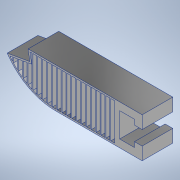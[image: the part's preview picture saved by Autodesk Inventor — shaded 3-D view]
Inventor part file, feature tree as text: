
AUTODESK INVENTOR PART (.ipt)
format: ipt  version: 2022 (Build 260153000, 153)  size: 371,200 bytes
history: native  units: mm
features: extrude x5, sketch x4, fillet x1, shell x1, projected_geometry x1
ambient origin geometry x8: Origin, YZ Plane, XZ Plane, XY Plane, X Axis, Y Axis, Z Axis, Center Point
bodies: Body1 (feature_tree)
feature tree (12):
  extrude  "Extrusion2"  Depth=5.8mm
  extrude  "Extrusion5"  Depth=12.0mm TaperAngle=0.0deg
  fillet  "Fillet2"  Radius=45.0mm
  shell  "Shell1"  Thickness=15.6mm
  extrude  "Extrusion7"  TaperAngle=0.0deg  [1 undecoded]
  extrude  "Extrusion8"  Depth=9.6mm
  extrude  "Extrusion9"  Depth=1.525mm
  sketch  "Sketch8"  dims[d41=5.8mm d48=44.0mm]
  sketch  "Sketch13"  dims[d50=3.0mm d56=12.0mm d57=0.0mm d63=45.0mm d67=15.6mm d71=0.0mm]
  sketch  "Sketch14"  dims[d80=17.453293mm d82=0.0mm d83=0.0mm]
  projected_geometry  "Projected Loop1"
  sketch  "Sketch15"  dims[d87=5.6mm d88=9.6mm d95=4.0mm d96=9.0mm d97=15.6mm d98=23.0mm d99=0.62mm d100=12.0mm d101=0.0mm d102=10.747401mm d103=12.0mm d104=0.0mm d105=0.38mm d107=0.38mm d1=0.38mm d108=0.38mm d109=0.38mm d110=0.38mm d111=0.38mm d112=0.38mm d113=0.38mm d118=0.38mm d120=3.81mm d121=3.81mm d122=3.81mm d123=3.81mm d124=3.81mm d125=3.81mm d127=12.0mm d128=0.0mm d129=0.38mm d131=0.38mm d132=0.38mm d133=0.38mm d134=0.38mm d135=0.38mm d136=0.38mm d137=0.38mm d138=0.38mm d139=0.38mm d140=0.38mm d180=1.525mm d189=1.525mm d190=1.525mm d191=0.38mm d192=1.525mm d193=1.525mm d194=1.525mm d195=1.525mm d196=1.525mm d197=1.525mm d198=1.525mm d199=1.525mm d200=1.525mm d201=1.525mm d202=1.525mm d203=1.525mm]
note: 1 required parameter value undecoded (feature->parameter linkage not recoverable at this tier; creation-order binding heuristic only, values carry confidence <= 0.55)
